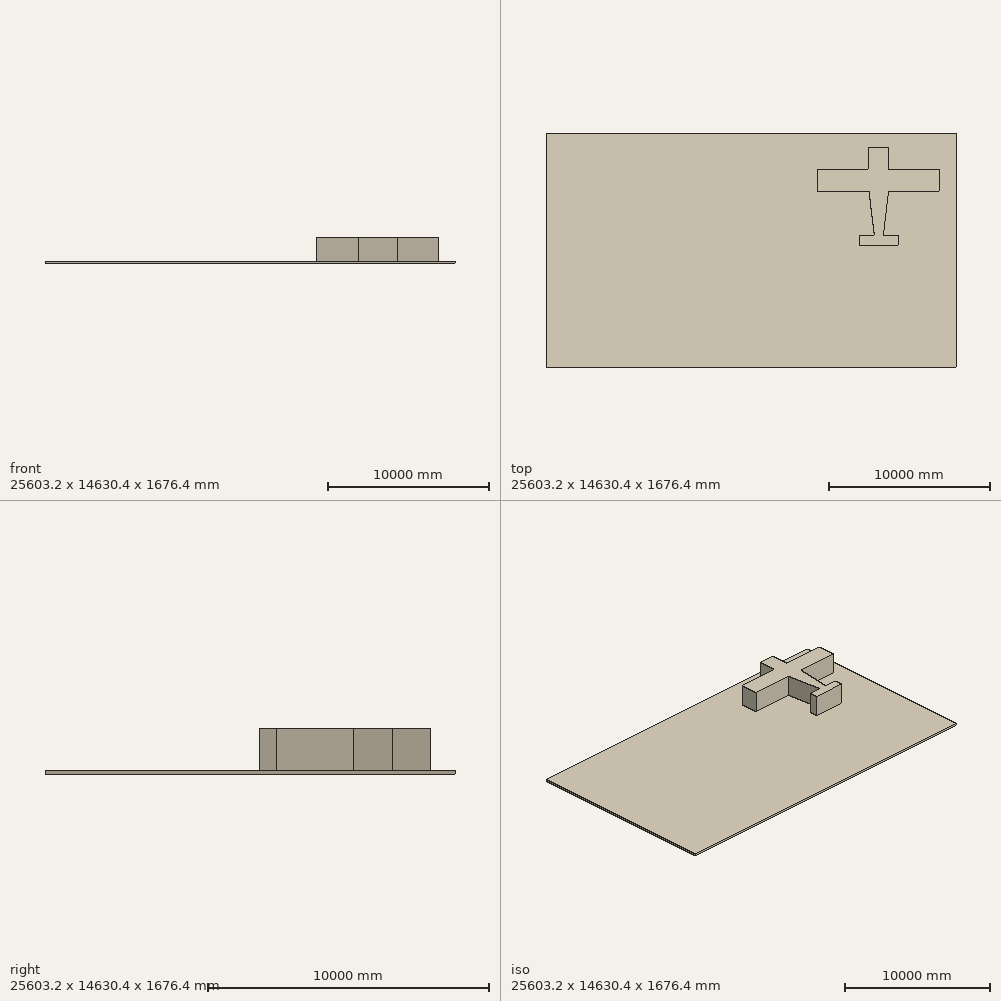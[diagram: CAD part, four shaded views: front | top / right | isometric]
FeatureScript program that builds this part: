
annotation { "Feature Type Name" : "Feature", "Feature Type Description" : "" }
export const myFeature = defineFeature(function(context is Context, id is Id, definition is map)
    precondition{}
    {
        {
            var Q0;
            Q0=qCreatedBy(makeId("Top.planeOp"),FACE);
            var sketch = newSketch(context, id + "F0", { "sketchPlane" : qUnion([Q0])});
            skLineSegment(sketch, "E0.bottom", {"start": v(0, 0) * mm, "end": v(25603.2, 0) * mm});
            skLineSegment(sketch, "E0.top", {"start": v(0, 14630.4) * mm, "end": v(25603.2, 14630.4) * mm});
            skLineSegment(sketch, "E0.left", {"start": v(0, 0) * mm, "end": v(0, 14630.4) * mm});
            skLineSegment(sketch, "E0.right", {"start": v(25603.2, 0) * mm, "end": v(25603.2, 14630.4) * mm});
            skSolve(sketch);
        }
        {
            var Q0;
            Q0=makeQuery(id+"F0.imprint","IMPRINT",FACE,{"disambiguationData":[TD([[makeQuery(id+"F0.imprint","IMPRINT",EDGE,{"derivedFrom":sQuery(id+"F0.wireOp",EDGE,"E0.bottom")}),1.0]])]});
            extrude(context, id + "F1", {"entities" : qUnion([Q0]), "oppositeDirection" : true, "depth" : 152.4 * mm});
        }
        {
            var Q0;
            Q0=makeQuery(id+"F1.opExtrude","SWEPT_FACE",FACE,{"disambiguationData":[OSD([sQuery(id+"F0.wireOp",EDGE,"E0.bottom")])]});
            var sketch = newSketch(context, id + "F2", { "sketchPlane" : qUnion([Q0])});
            skSolve(sketch);
        }
        {
            var Q0;
            Q0=qCreatedBy(makeId("Top.planeOp"),FACE);
            var sketch = newSketch(context, id + "F3", { "sketchPlane" : qUnion([Q0])});
            skLineSegment(sketch, "E1", {"start": v(17277.16, 14085.42) * mm, "end": v(17277.16, 4941.42) * mm, "construction": true});
            skLineSegment(sketch, "E2", {"start": v(17277.16, 7660.69) * mm, "end": v(23373.16, 7660.69) * mm, "construction": true});
            skLineSegment(sketch, "E3", {"start": v(17277.16, 13419.86) * mm, "end": v(19105.96, 13419.86) * mm, "construction": true});
            skLineSegment(sketch, "E4", {"start": v(17277.16, 4941.42) * mm, "end": v(18039.16, 4941.42) * mm});
            skLineSegment(sketch, "E5", {"start": v(18039.16, 4941.42) * mm, "end": v(18039.16, 7075.02) * mm});
            skLineSegment(sketch, "E6", {"start": v(18039.16, 7075.02) * mm, "end": v(23373.16, 7075.02) * mm});
            skLineSegment(sketch, "E7", {"start": v(23373.16, 7075.02) * mm, "end": v(23373.16, 8599.02) * mm});
            skLineSegment(sketch, "E8", {"start": v(23373.16, 8599.02) * mm, "end": v(18039.16, 8599.02) * mm});
            skLineSegment(sketch, "E9", {"start": v(18039.16, 8599.02) * mm, "end": v(17557.95, 13033.25) * mm});
            skLineSegment(sketch, "E10", {"start": v(17557.95, 13033.25) * mm, "end": v(19105.96, 13033.25) * mm});
            skLineSegment(sketch, "E11", {"start": v(19105.96, 13033.25) * mm, "end": v(19105.96, 13793.14) * mm});
            skLineSegment(sketch, "E12", {"start": v(19105.96, 13793.14) * mm, "end": v(17557.95, 13793.14) * mm});
            skLineSegment(sketch, "E13", {"start": v(17557.95, 13793.14) * mm, "end": v(17277.16, 14085.42) * mm});
            skLineSegment(sketch, "E14.MirrorCS", {"start": v(16996.37, 13793.14) * mm, "end": v(17277.16, 14085.42) * mm});
            skLineSegment(sketch, "E15.MirrorCS", {"start": v(11181.16, 8599.02) * mm, "end": v(16515.16, 8599.02) * mm});
            skLineSegment(sketch, "E16.MirrorCS", {"start": v(11181.16, 7075.02) * mm, "end": v(11181.16, 8599.02) * mm});
            skLineSegment(sketch, "E17.MirrorCS", {"start": v(16515.16, 8599.02) * mm, "end": v(16996.37, 13033.25) * mm});
            skLineSegment(sketch, "E18.MirrorCS", {"start": v(16996.37, 13033.25) * mm, "end": v(15448.36, 13033.25) * mm});
            skLineSegment(sketch, "E19.MirrorCS", {"start": v(16515.16, 7075.02) * mm, "end": v(11181.16, 7075.02) * mm});
            skLineSegment(sketch, "E20.MirrorCS", {"start": v(15448.36, 13793.14) * mm, "end": v(16996.37, 13793.14) * mm});
            skLineSegment(sketch, "E21.MirrorCS", {"start": v(17277.16, 7660.69) * mm, "end": v(11181.16, 7660.69) * mm, "construction": true});
            skLineSegment(sketch, "E22.MirrorCS", {"start": v(17277.16, 13419.86) * mm, "end": v(15448.36, 13419.86) * mm, "construction": true});
            skLineSegment(sketch, "E23.MirrorCS", {"start": v(16515.16, 4941.42) * mm, "end": v(16515.16, 7075.02) * mm});
            skLineSegment(sketch, "E24.MirrorCS", {"start": v(15448.36, 13033.25) * mm, "end": v(15448.36, 13793.14) * mm});
            skLineSegment(sketch, "E25.MirrorCS", {"start": v(17277.16, 4941.42) * mm, "end": v(16515.16, 4941.42) * mm});
            skLineSegment(sketch, "E26.0", {"start": v(17557.95, 13033.25) * mm, "end": v(17557.95, 13793.14) * mm, "construction": true});
            skLineSegment(sketch, "E27.0", {"start": v(19105.96, 13033.25) * mm, "end": v(19105.96, 13419.86) * mm, "construction": true});
            skLineSegment(sketch, "E28.0", {"start": v(18039.16, 4941.42) * mm, "end": v(18039.16, 8599.02) * mm, "construction": true});
            skLineSegment(sketch, "E29.0", {"start": v(23373.16, 7075.02) * mm, "end": v(23373.16, 7660.69) * mm, "construction": true});
            skSolve(sketch);
        }
        {
            var Q0;
            Q0=qCreatedBy(makeId("Top.planeOp"),FACE);
            var sketch = newSketch(context, id + "F4", { "sketchPlane" : qUnion([Q0])});
            skLineSegment(sketch, "E30", {"start": v(20745.8, 13742.4) * mm, "end": v(20755.84, 7646.41) * mm, "construction": true});
            skLineSegment(sketch, "E31", {"start": v(20748.95, 11828.47) * mm, "end": v(16938.95, 11822.2) * mm, "construction": true});
            skLineSegment(sketch, "E32", {"start": v(20745.8, 13742.4) * mm, "end": v(20136.2, 13741.4) * mm});
            skLineSegment(sketch, "E33", {"start": v(20136.2, 13741.4) * mm, "end": v(20138.45, 12369.8) * mm});
            skLineSegment(sketch, "E34", {"start": v(20138.45, 12369.8) * mm, "end": v(16939.3, 12364.53) * mm});
            skLineSegment(sketch, "E35", {"start": v(16939.3, 12364.53) * mm, "end": v(16940.32, 10992.93) * mm});
            skLineSegment(sketch, "E36", {"start": v(16940.32, 10992.93) * mm, "end": v(20140.72, 10995.3) * mm});
            skLineSegment(sketch, "E37", {"start": v(20140.72, 10995.3) * mm, "end": v(20470.1, 8255.54) * mm});
            skLineSegment(sketch, "E38", {"start": v(20470.1, 8255.54) * mm, "end": v(19535.63, 8254) * mm});
            skLineSegment(sketch, "E39", {"start": v(19535.63, 8254) * mm, "end": v(19536.64, 7644.4) * mm});
            skLineSegment(sketch, "E40", {"start": v(19536.64, 7644.4) * mm, "end": v(20755.84, 7646.41) * mm});
            skLineSegment(sketch, "E41.MirrorCS", {"start": v(21975.04, 7648.42) * mm, "end": v(20755.84, 7646.41) * mm});
            skLineSegment(sketch, "E42.MirrorCS", {"start": v(20745.8, 13742.4) * mm, "end": v(21355.4, 13743.4) * mm});
            skLineSegment(sketch, "E43.MirrorCS", {"start": v(24556.8, 12377.08) * mm, "end": v(24560.3, 11005.48) * mm});
            skLineSegment(sketch, "E44.MirrorCS", {"start": v(24560.3, 11005.48) * mm, "end": v(21359.92, 10997.31) * mm});
            skLineSegment(sketch, "E45.MirrorCS", {"start": v(21355.4, 13743.4) * mm, "end": v(21357.65, 12371.81) * mm});
            skLineSegment(sketch, "E46.MirrorCS", {"start": v(21039.56, 8256.48) * mm, "end": v(21974.03, 8258.02) * mm});
            skLineSegment(sketch, "E47.MirrorCS", {"start": v(21357.65, 12371.81) * mm, "end": v(24556.8, 12377.08) * mm});
            skLineSegment(sketch, "E48.MirrorCS", {"start": v(21359.92, 10997.31) * mm, "end": v(21039.56, 8256.48) * mm});
            skLineSegment(sketch, "E49.MirrorCS", {"start": v(21974.03, 8258.02) * mm, "end": v(21975.04, 7648.42) * mm});
            skLineSegment(sketch, "E50.0", {"start": v(19535.63, 8254) * mm, "end": v(19536.64, 7644.4) * mm, "construction": true});
            skLineSegment(sketch, "E51.0", {"start": v(20138.45, 12369.8) * mm, "end": v(20140.72, 10995.3) * mm, "construction": true});
            skLineSegment(sketch, "E52.0", {"start": v(16938.95, 11822.2) * mm, "end": v(16940.32, 10992.93) * mm, "construction": true});
            skSolve(sketch);
        }
        {
            var Q0;
            Q0=makeQuery(id+"F4.imprint","IMPRINT",FACE,{"disambiguationData":[TD([[makeQuery(id+"F4.imprint","IMPRINT",EDGE,{"derivedFrom":sQuery(id+"F4.wireOp",EDGE,"E32")}),1.0]])]});
            extrude(context, id + "F5", {"entities" : qUnion([Q0]), "operationType" : NewBodyOperationType.ADD, "depth" : 1524 * mm});
        }
    });
